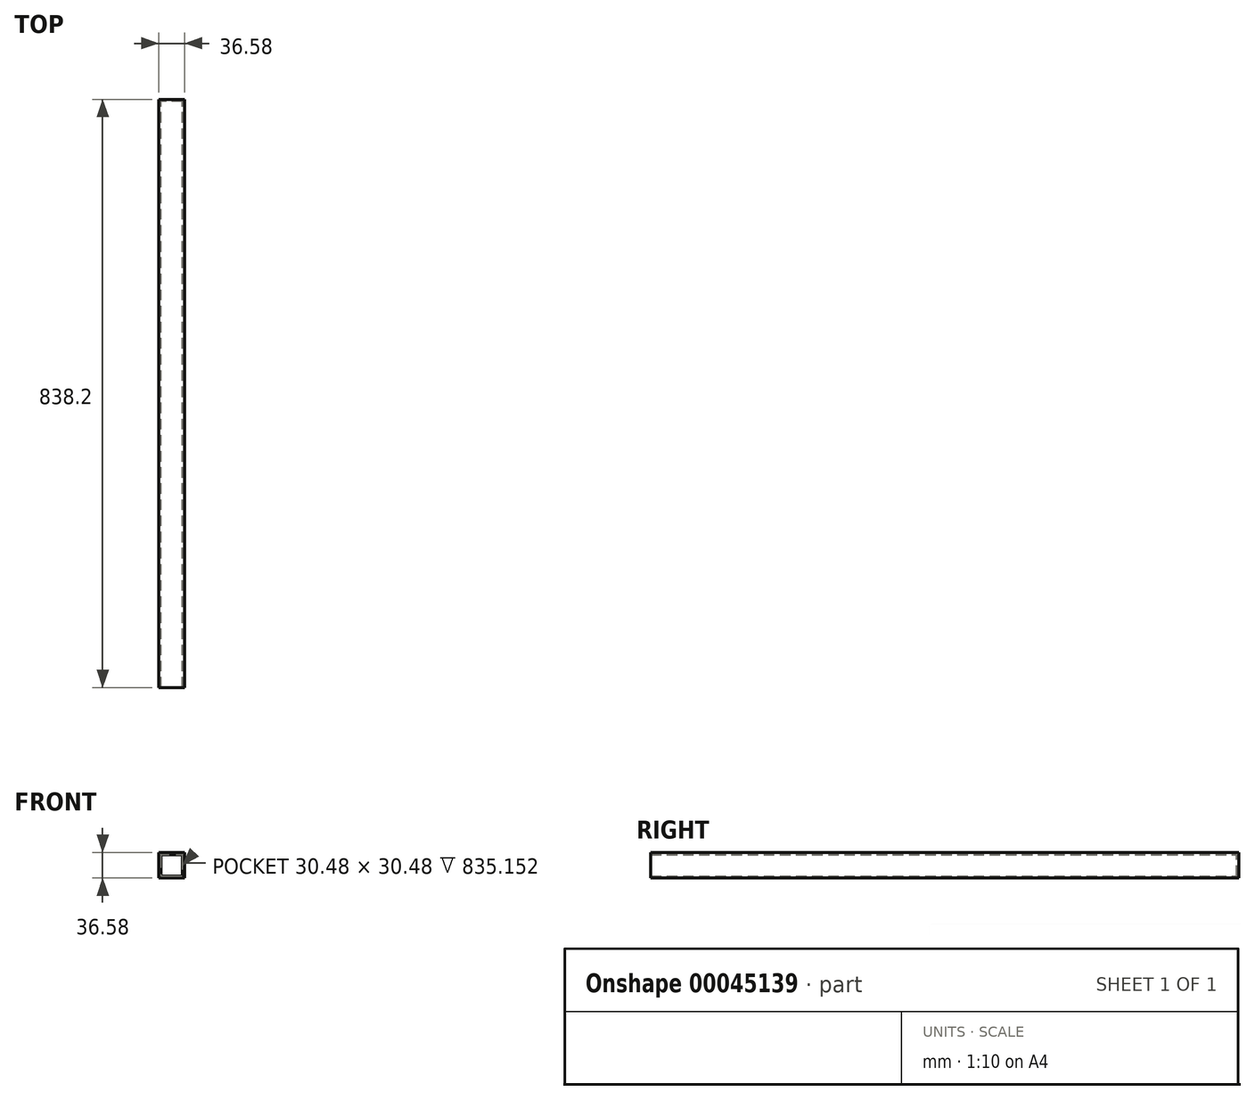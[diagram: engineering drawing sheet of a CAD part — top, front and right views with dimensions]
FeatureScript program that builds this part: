
annotation { "Feature Type Name" : "Feature", "Feature Type Description" : "" }
export const myFeature = defineFeature(function(context is Context, id is Id, definition is map)
    precondition{}
    {
        {
            var Q0;
            Q0=qCreatedBy(makeId("Front.planeOp"),FACE);
            var sketch = newSketch(context, id + "F0", { "sketchPlane" : qUnion([Q0])});
            skLineSegment(sketch, "E0.rect.bottom", {"start": v(18.29, -18.29) * mm, "end": v(-18.29, -18.29) * mm});
            skLineSegment(sketch, "E0.rect.top", {"start": v(18.29, 18.29) * mm, "end": v(-18.29, 18.29) * mm});
            skLineSegment(sketch, "E0.rect.left", {"start": v(18.29, -18.29) * mm, "end": v(18.29, 18.29) * mm});
            skLineSegment(sketch, "E0.rect.right", {"start": v(-18.29, -18.29) * mm, "end": v(-18.29, 18.29) * mm});
            skPoint(sketch, "E0.rect.middle", {"position": v(0, 0) * mm});
            skSolve(sketch);
        }
        {
            var Q0;
            Q0=makeQuery(id+"F0.imprint","IMPRINT",FACE,{"disambiguationData":[TD([[makeQuery(id+"F0.imprint","IMPRINT",EDGE,{"derivedFrom":sQuery(id+"F0.wireOp",EDGE,"E0.rect.bottom")}),-1.0]])]});
            extrude(context, id + "F1", {"entities" : qUnion([Q0]), "depth" : 838.2 * mm});
        }
        {
            var Q0;
            Q0=makeQuery(id+"F1.opExtrude","CAP_FACE",FACE,{"disambiguationData":[OSD([sQuery(id+"F0.wireOp",EDGE,"E0.rect.bottom"),sQuery(id+"F0.wireOp",EDGE,"E0.rect.top"),sQuery(id+"F0.wireOp",EDGE,"E0.rect.left"),sQuery(id+"F0.wireOp",EDGE,"E0.rect.right")])],"isStart":false});
            shell(context, id + "F2", {"entities" : qUnion([Q0]), "thickness" : 3.05 * mm});
        }
    });
